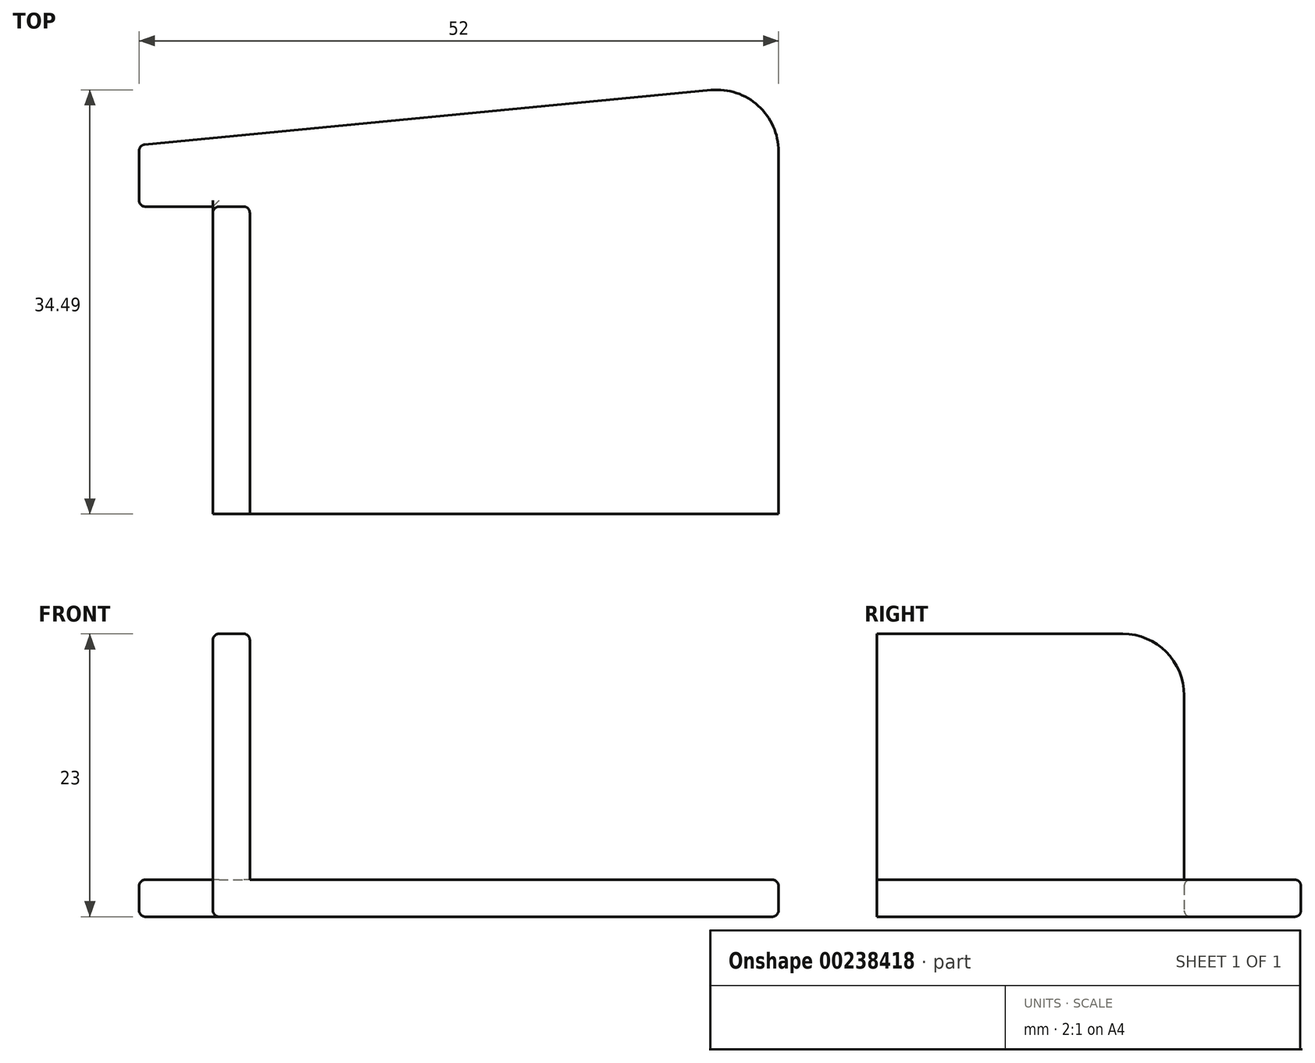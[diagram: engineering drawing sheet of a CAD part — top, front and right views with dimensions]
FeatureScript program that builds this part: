
annotation { "Feature Type Name" : "Feature", "Feature Type Description" : "" }
export const myFeature = defineFeature(function(context is Context, id is Id, definition is map)
    precondition{}
    {
        {
            var Q0;
            Q0=qCreatedBy(makeId("Top.planeOp"),FACE);
            var sketch = newSketch(context, id + "F0", { "sketchPlane" : qUnion([Q0])});
            skLineSegment(sketch, "E0", {"start": v(-20.55, 9.84) * mm, "end": v(-20.55, 4.84) * mm});
            skLineSegment(sketch, "E1", {"start": v(-20.55, 4.84) * mm, "end": v(-14.55, 4.84) * mm});
            skLineSegment(sketch, "E2", {"start": v(-14.55, 4.84) * mm, "end": v(-14.55, -20.16) * mm});
            skLineSegment(sketch, "E3", {"start": v(-14.55, -20.16) * mm, "end": v(31.45, -20.16) * mm});
            skLineSegment(sketch, "E4", {"start": v(31.45, -20.16) * mm, "end": v(31.45, 9.33) * mm});
            skLineSegment(sketch, "E5", {"start": v(-20.55, 9.84) * mm, "end": v(25.97, 14.31) * mm});
            skPoint(sketch, "E6.visualSharp", {"position": v(31.45, 14.84) * mm});
            skArc(sketch, "E6.filletArc", {"start": v(31.45, 9.33) * mm, "mid": v(29.8, 13.03) * mm, "end": v(25.97, 14.31) * mm});
            skLineSegment(sketch, "E7.bottom", {"start": v(-14.55, 4.84) * mm, "end": v(-11.55, 4.84) * mm});
            skLineSegment(sketch, "E7.top", {"start": v(-14.55, -20.16) * mm, "end": v(-11.55, -20.16) * mm});
            skLineSegment(sketch, "E7.right", {"start": v(-11.55, 4.84) * mm, "end": v(-11.55, -20.16) * mm});
            skSolve(sketch);
        }
        {
            var Q0;
            Q0=makeQuery(id+"F0.imprint","IMPRINT",FACE,{"disambiguationData":[TD([[makeQuery(id+"F0.imprint","IMPRINT",EDGE,{"derivedFrom":sQuery(id+"F0.wireOp",EDGE,"E0")}),1.0]])]});
            extrude(context, id + "F1", {"entities" : qUnion([Q0]), "depth" : 3 * mm, "offsetDistance" : 25 * mm});
        }
        {
            var Q0;
            {var subQ0=sQuery(id+"F0.wireOp",EDGE,"E2");Q0=makeQuery(id+"F0.imprint","IMPRINT",FACE,{"disambiguationData":[TD([[makeQuery(id+"F0.imprint","IMPRINT",EDGE,{"derivedFrom":subQ0}),1.0]])]});}
            extrude(context, id + "F2", {"entities" : qUnion([Q0]), "operationType" : NewBodyOperationType.ADD, "depth" : 23 * mm, "offsetDistance" : 25 * mm});
        }
        {
            var Q0;
            Q0=makeQuery(id+"F1.opExtrude","CAP_EDGE",EDGE,{"disambiguationData":[OSD([sQuery(id+"F0.wireOp",EDGE,"E5")])],"isStart":true});
            var Q1;
            Q1=makeQuery(id+"F1.opExtrude","CAP_EDGE",EDGE,{"disambiguationData":[OSD([sQuery(id+"F0.wireOp",EDGE,"E5")])],"isStart":false});
            var Q2;
            Q2=makeQuery(id+"F1.opExtrude","SWEPT_EDGE",EDGE,{"disambiguationData":[OSD([sQuery(id+"F0.wireOp",EDGE,"E0"),sQuery(id+"F0.wireOp",EDGE,"E5")])]});
            var Q3;
            Q3=makeQuery(id+"F1.opExtrude","CAP_EDGE",EDGE,{"disambiguationData":[OSD([sQuery(id+"F0.wireOp",EDGE,"E6.filletArc")])],"isStart":false});
            var Q4;
            Q4=makeQuery(id+"F1.opExtrude","CAP_EDGE",EDGE,{"disambiguationData":[OSD([sQuery(id+"F0.wireOp",EDGE,"E4")])],"isStart":false});
            var Q5;
            Q5=makeQuery(id+"F1.opExtrude","CAP_EDGE",EDGE,{"disambiguationData":[OSD([sQuery(id+"F0.wireOp",EDGE,"E6.filletArc")])],"isStart":true});
            var Q6;
            Q6=makeQuery(id+"F1.opExtrude","CAP_EDGE",EDGE,{"disambiguationData":[OSD([sQuery(id+"F0.wireOp",EDGE,"E4")])],"isStart":true});
            fillet(context, id + "F3", {"entities" : qUnion([Q0, Q1, Q2, Q3, Q4, Q5, Q6]), "radius" : .5 * mm, "tangentPropagation" : true, "allowEdgeOverflow" : false});
        }
        {
            var Q0;
            Q0=makeQuery(id+"F1.opExtrude","CAP_EDGE",EDGE,{"disambiguationData":[OSD([sQuery(id+"F0.wireOp",EDGE,"E7.right")])],"isStart":false});
            var Q1;
            {var subQ0=sQuery(id+"F0.wireOp",EDGE,"E7.bottom");var subQ1=sQuery(id+"F0.wireOp",EDGE,"E1");Q1=makeQuery(id+"F2.boolean.opBoolean","SPLIT",EDGE,{"disambiguationData":[topologyDisambiguationEdgeConnected([makeQuery(id+"F2.opExtrude","SWEPT_FACE",FACE,{"disambiguationData":[OSD([subQ0])]})])],"derivedFrom":makeQuery(id+"F1.opExtrude","CAP_EDGE",EDGE,{"disambiguationData":[OSD([subQ1,subQ0])],"isStart":false})});}
            fillet(context, id + "F4", {"entities" : qUnion([Q0, Q1]), "radius" : .5 * mm, "tangentPropagation" : true, "allowEdgeOverflow" : false});
        }
        {
            var Q0;
            Q0=makeQuery(id+"F2.opExtrude","CAP_EDGE",EDGE,{"disambiguationData":[OSD([sQuery(id+"F0.wireOp",EDGE,"E7.right")])],"isStart":false});
            var Q1;
            Q1=makeQuery(id+"F2.opExtrude","SWEPT_EDGE",EDGE,{"disambiguationData":[OSD([sQuery(id+"F0.wireOp",EDGE,"E7.bottom"),sQuery(id+"F0.wireOp",EDGE,"E7.right")])]});
            var Q2;
            Q2=makeQuery(id+"F2.opExtrude","CAP_EDGE",EDGE,{"disambiguationData":[OSD([sQuery(id+"F0.wireOp",EDGE,"E2")])],"isStart":false});
            var Q3;
            {var subQ0=sQuery(id+"F0.wireOp",EDGE,"E2");var subQ1=sQuery(id+"F0.wireOp",EDGE,"E7.bottom");Q3=makeQuery(id+"F2.boolean.opBoolean","SPLIT",EDGE,{"disambiguationData":[topologyDisambiguationEdgeConnected([makeQuery(id+"F2.opExtrude","SWEPT_FACE",FACE,{"disambiguationData":[OSD([subQ1])]})])],"derivedFrom":makeQuery(id+"F2.opExtrude","SWEPT_EDGE",EDGE,{"disambiguationData":[OSD([sQuery(id+"F0.wireOp",EDGE,"E1"),subQ0,subQ1])]})});}
            fillet(context, id + "F5", {"entities" : qUnion([Q0, Q1, Q2, Q3]), "radius" : .5 * mm, "tangentPropagation" : true, "allowEdgeOverflow" : false});
        }
        {
            var Q0;
            Q0=makeQuery(id+"F1.opExtrude","CAP_EDGE",EDGE,{"disambiguationData":[OSD([sQuery(id+"F0.wireOp",EDGE,"E1"),sQuery(id+"F0.wireOp",EDGE,"E7.bottom")])],"isStart":true});
            var Q1;
            Q1=makeQuery(id+"F1.opExtrude","CAP_EDGE",EDGE,{"disambiguationData":[OSD([sQuery(id+"F0.wireOp",EDGE,"E0")])],"isStart":true});
            var Q2;
            {var subQ0=sQuery(id+"F0.wireOp",EDGE,"E7.bottom");var subQ1=sQuery(id+"F0.wireOp",EDGE,"E1");Q2=makeQuery(id+"F2.boolean.opBoolean","SPLIT",EDGE,{"disambiguationData":[topologyDisambiguationEdgeConnected([makeQuery(id+"F1.opExtrude","SWEPT_FACE",FACE,{"disambiguationData":[OSD([subQ1,subQ0])]})])],"derivedFrom":makeQuery(id+"F1.opExtrude","CAP_EDGE",EDGE,{"disambiguationData":[OSD([subQ1,subQ0])],"isStart":false})});}
            var Q3;
            Q3=makeQuery(id+"F1.opExtrude","CAP_EDGE",EDGE,{"disambiguationData":[OSD([sQuery(id+"F0.wireOp",EDGE,"E0")])],"isStart":false});
            var Q4;
            Q4=makeQuery(id+"F1.opExtrude","SWEPT_EDGE",EDGE,{"disambiguationData":[OSD([sQuery(id+"F0.wireOp",EDGE,"E0"),sQuery(id+"F0.wireOp",EDGE,"E1")])]});
            fillet(context, id + "F6", {"entities" : qUnion([Q0, Q1, Q2, Q3, Q4]), "radius" : .5 * mm, "tangentPropagation" : true, "allowEdgeOverflow" : false});
        }
        {
            var Q0;
            Q0=makeQuery(id+"F2.opExtrude","CAP_EDGE",EDGE,{"disambiguationData":[OSD([sQuery(id+"F0.wireOp",EDGE,"E2")])],"isStart":true});
            fillet(context, id + "F7", {"entities" : qUnion([Q0]), "radius" : .5 * mm, "tangentPropagation" : true, "allowEdgeOverflow" : false});
        }
        {
            var Q0;
            Q0=makeQuery(id+"F2.opExtrude","CAP_EDGE",EDGE,{"disambiguationData":[OSD([sQuery(id+"F0.wireOp",EDGE,"E7.bottom")])],"isStart":false});
            fillet(context, id + "F8", {"entities" : qUnion([Q0]), "radius" : 5 * mm, "tangentPropagation" : true, "allowEdgeOverflow" : false});
        }
    });
